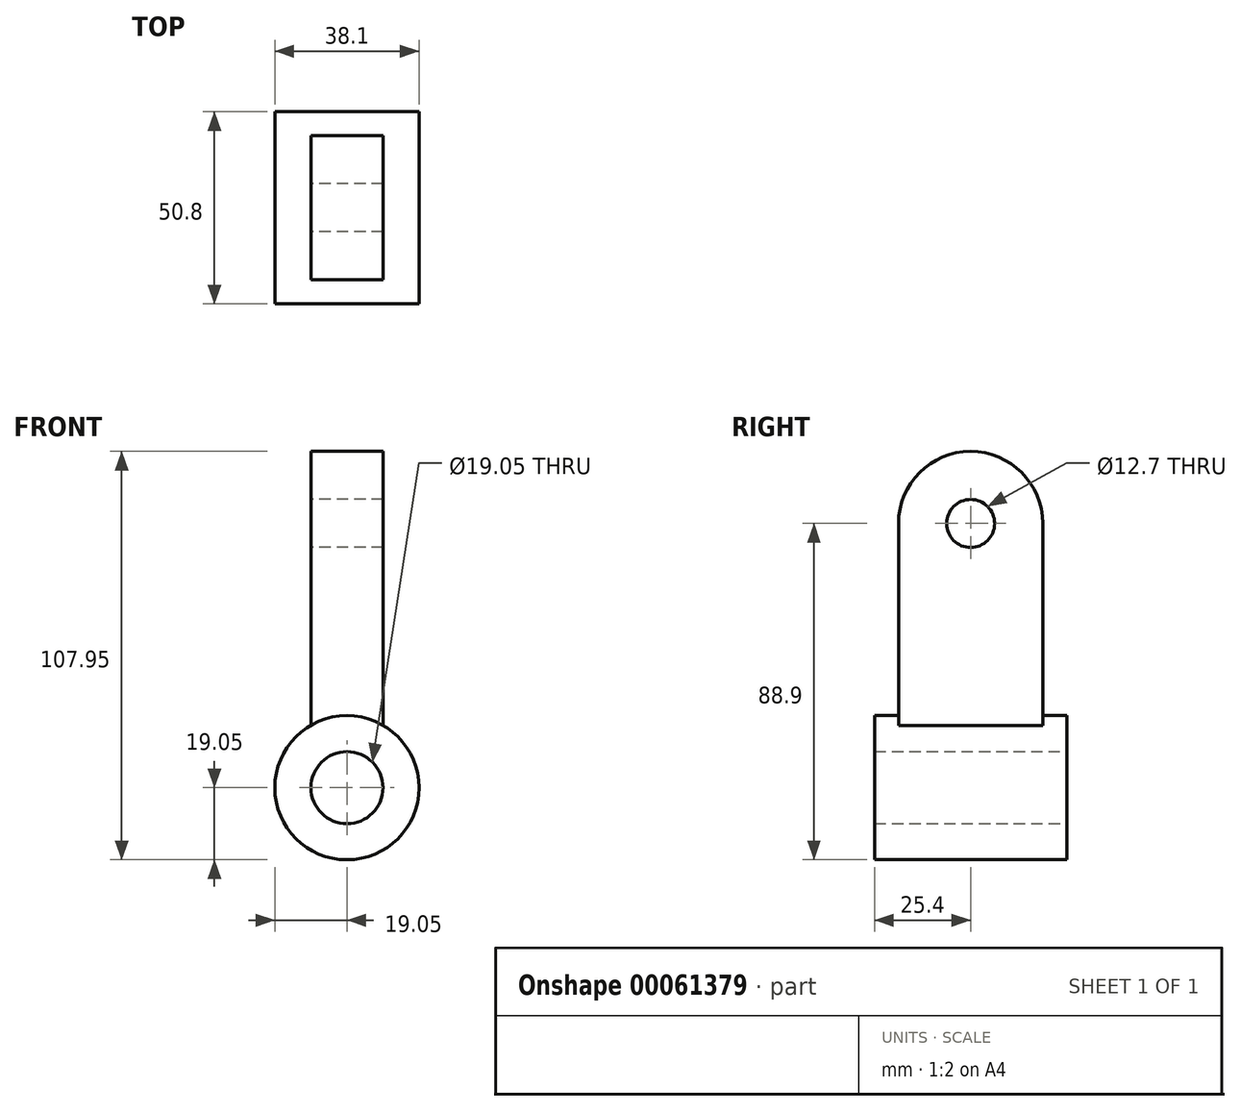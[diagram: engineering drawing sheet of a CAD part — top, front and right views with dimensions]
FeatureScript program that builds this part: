
annotation { "Feature Type Name" : "Feature", "Feature Type Description" : "" }
export const myFeature = defineFeature(function(context is Context, id is Id, definition is map)
    precondition{}
    {
        {
            var Q0;
            Q0=qCreatedBy(makeId("Front.planeOp"),FACE);
            var sketch = newSketch(context, id + "F0", { "sketchPlane" : qUnion([Q0])});
            skCircle(sketch, "E0", {"center": v(0, 0) * mm, "radius": 9.53 * mm});
            skCircle(sketch, "E1", {"center": v(0, 0) * mm, "radius": 19.05 * mm});
            skSolve(sketch);
        }
        {
            var Q0;
            Q0 = qSketchRegion(id + "F0", true);
            extrude(context, id + "F1", {"entities" : qUnion([Q0]), "depth" : 25.4 * mm, "hasSecondDirection" : true, "secondDirectionOppositeDirection" : true, "secondDirectionDepth" : 25.4 * mm});
        }
        {
            var Q0;
            Q0=qCreatedBy(makeId("Right.planeOp"),FACE);
            var sketch = newSketch(context, id + "F2", { "sketchPlane" : qUnion([Q0])});
            skLineSegment(sketch, "E2", {"start": v(0, 0) * mm, "end": v(0, 69.85) * mm, "construction": true});
            skCircle(sketch, "E3", {"center": v(0, 69.85) * mm, "radius": 6.35 * mm});
            skLineSegment(sketch, "E4", {"start": v(-19.05, 12.7) * mm, "end": v(19.05, 12.7) * mm});
            skLineSegment(sketch, "E5", {"start": v(19.05, 12.7) * mm, "end": v(19.05, 69.85) * mm});
            skLineSegment(sketch, "E6", {"start": v(-19.05, 12.7) * mm, "end": v(-19.05, 69.85) * mm});
            skArc(sketch, "E7", {"start": v(-19.05, 69.85) * mm, "mid": v(0, 88.9) * mm, "end": v(19.05, 69.85) * mm});
            skSolve(sketch);
        }
        {
            var Q0;
            Q0 = qSketchRegion(id + "F2", true);
            extrude(context, id + "F3", {"entities" : qUnion([Q0]), "operationType" : NewBodyOperationType.ADD, "depth" : 9.52 * mm, "hasSecondDirection" : true, "secondDirectionOppositeDirection" : true, "secondDirectionDepth" : 9.52 * mm});
        }
    });
